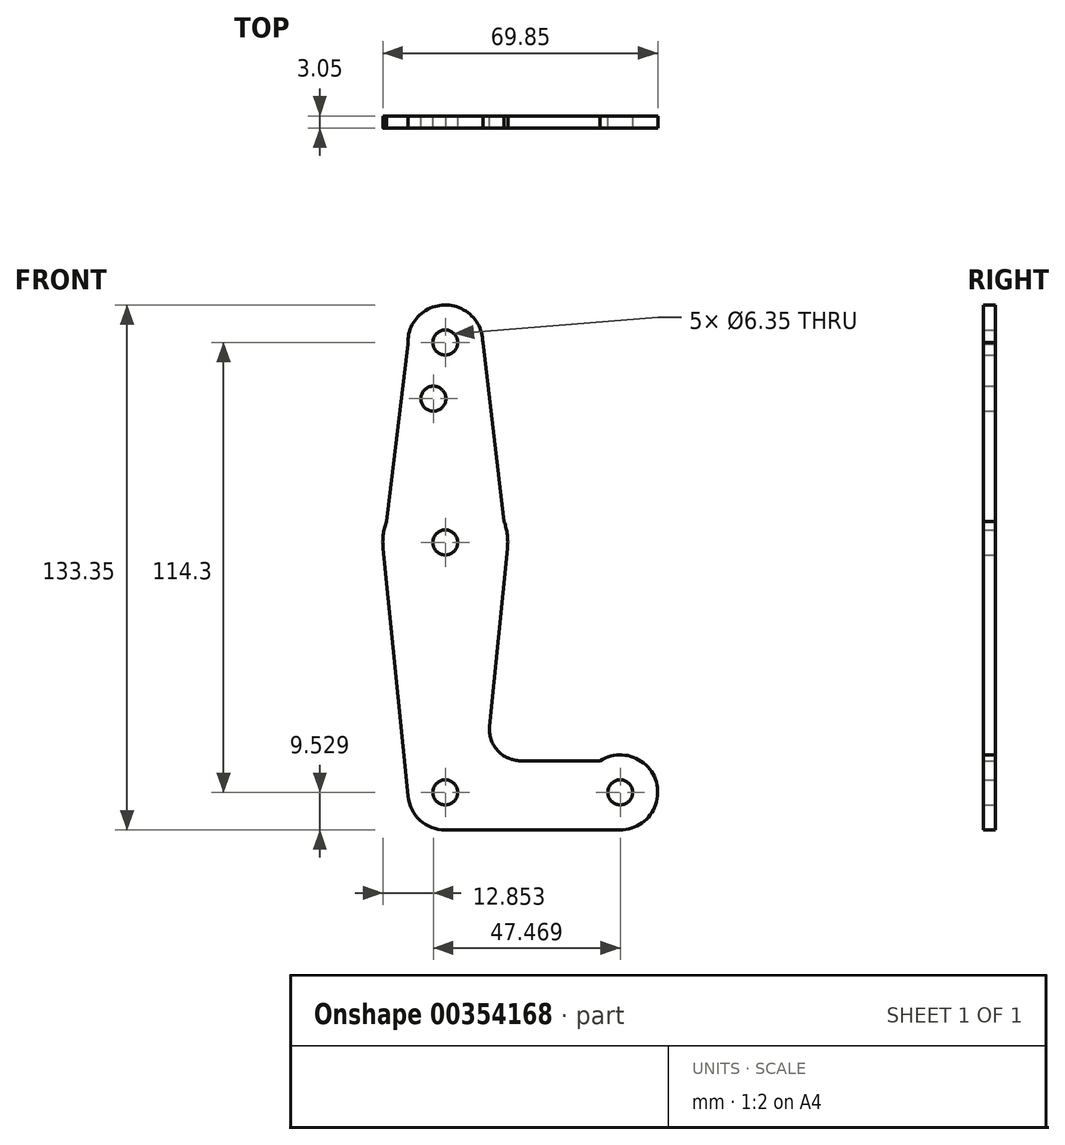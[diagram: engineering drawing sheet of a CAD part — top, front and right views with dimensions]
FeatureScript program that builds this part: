
annotation { "Feature Type Name" : "Feature", "Feature Type Description" : "" }
export const myFeature = defineFeature(function(context is Context, id is Id, definition is map)
    precondition{}
    {
        {
            var Q0;
            Q0=qCreatedBy(makeId("Front.planeOp"),FACE);
            var sketch = newSketch(context, id + "F0", { "sketchPlane" : qUnion([Q0])});
            skLineSegment(sketch, "E0", {"start": v(-55.1, 89.17) * mm, "end": v(-55.1, -25.13) * mm});
            skLineSegment(sketch, "E1", {"start": v(-55.1, -25.13) * mm, "end": v(-10.65, -25.13) * mm});
            skCircle(sketch, "E2", {"center": v(-55.1, 89.17) * mm, "radius": 9.53 * mm});
            skCircle(sketch, "E3", {"center": v(-55.1, 38.37) * mm, "radius": 15.88 * mm});
            skCircle(sketch, "E4", {"center": v(-55.1, -25.13) * mm, "radius": 9.53 * mm});
            skCircle(sketch, "E5", {"center": v(-10.65, -25.13) * mm, "radius": 9.53 * mm});
            skLineSegment(sketch, "E6", {"start": v(-70.9, 36.78) * mm, "end": v(-64.58, -26.08) * mm});
            skLineSegment(sketch, "E7", {"start": v(-39.3, 36.78) * mm, "end": v(-43.84, -8.34) * mm});
            skLineSegment(sketch, "E8", {"start": v(-64.58, 89.17) * mm, "end": v(-70.9, 36.78) * mm});
            skLineSegment(sketch, "E9", {"start": v(-45.57, 89.17) * mm, "end": v(-39.3, 36.78) * mm});
            skLineSegment(sketch, "E10", {"start": v(-55.1, -34.66) * mm, "end": v(-10.65, -34.66) * mm});
            skLineSegment(sketch, "E11", {"start": v(-35.93, -17.09) * mm, "end": v(-10.65, -17.09) * mm});
            skCircle(sketch, "E12", {"center": v(-55.1, 89.17) * mm, "radius": 3.18 * mm});
            skCircle(sketch, "E13", {"center": v(-55.1, 38.37) * mm, "radius": 3.18 * mm});
            skCircle(sketch, "E14", {"center": v(-55.1, -25.13) * mm, "radius": 3.18 * mm});
            skCircle(sketch, "E15", {"center": v(-10.65, -25.13) * mm, "radius": 3.18 * mm});
            skPoint(sketch, "E16.newPointB", {"position": v(-55.1, -17.09) * mm});
            skArc(sketch, "E16.filletArc", {"start": v(-43.84, -8.34) * mm, "mid": v(-41.82, -14.47) * mm, "end": v(-35.93, -17.09) * mm});
            skCircle(sketch, "E17", {"center": v(-58.12, 74.9) * mm, "radius": 3.18 * mm});
            skSolve(sketch);
        }
        {
            var Q0;
            Q0 = qSketchRegion(id + "F0", true);
            var Q1;
            {var subQ0=sQuery(id+"F0.wireOp",EDGE,"E4");var subQ1=sQuery(id+"F0.wireOp",EDGE,"E0");var subQ2=makeQuery(id+"F0.imprint","INTERSECT",VERTEX,{"derivedFrom":[subQ1,subQ0]});Q1=makeQuery(id+"F0.imprint","IMPRINT",FACE,{"disambiguationData":[TD([[makeQuery(id+"F0.imprint","IMPRINT",EDGE,{"disambiguationData":[TD([[subQ2,-1.0]])],"derivedFrom":subQ1}),1.0]])]});}
            extrude(context, id + "F1", {"entities" : qUnion([Q0, Q1]), "depth" : 3.05 * mm});
        }
    });
